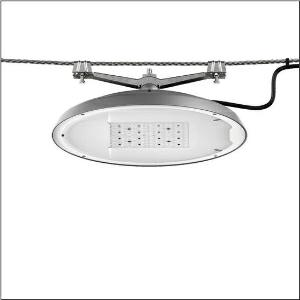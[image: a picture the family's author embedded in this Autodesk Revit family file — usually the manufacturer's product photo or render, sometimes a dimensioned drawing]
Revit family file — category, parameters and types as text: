
# Revit family: dl_r__50_iq_mini___st0_8s_5xa248v31f08me_3f47
name_source: partatom
category: Lighting Fixtures
units: mm (PartAtom-declared; Revit-internal decimal feet)

## family parameters
Cut with Voids When Loaded = No
Host = Face
Light Source = No
Part Type = Normal
Room Calculation Point = No
Round Connector Dimension = Use Diameter
Shared = No

## types (1)
- --- (1 x LED, 15660 lm, 107.8 W, 3000K)
    Apparent Load = 108 VA
    CIE Flux Codes = 38 75 97 100 100
    Color Rendering = 70
    Color Temperature = 3000K
    Default Elevation = 1800 mm
    Description = DL® 50 iQ mini, catenary luminaire, primary light control with lens, of PMMA, primary optical cover: cover, of toughened safety glass, transparent, light distribution: ST0.8s, light emission: direct distribution, primary light characteristic: symmetric, installation type: suspended mounting, LED, High Power LED, rated luminous flux: 15.660lm, luminous efficacy: 145lm/W, light colour: 730, colour temperature: 3000K, control: optimised constant luminous flux control (CLO 2.0), Desk-Remote (wireless, voltage-free reading and setting of iQ features in the workshop via application-optimized NFC function/RFID function), Light-Fading, Smart-Wire, Night-Set, Lumen-Switch, Temp-Guard, Auto-Match, Street-Remote, mains connection: 230..240V, AC, 50/60Hz, start of lifetime: 108W, end of service life: 118W, reduction: 47W, luminaire housing, of diecast aluminium, powder-coated, Siteco® metallic grey (DB 702S), diameter: 500mm, height: 115mm, protection rating (complete): IP66, insulation class (complete): insulation class II (safety insulation), certification: CE, ENEC, VDE, impact resistance: IK08, permissible operating ambient temperature for outdoor applications: -25..+40°C, standard-compliant lighting for roads and squares, packaging unit: 1 piece

Light Distribution: ST0.8s
    Height = 124 mm  [stored 0.406824 ft]
    Lamp = 1 x LED
    Lamp Light Flux = 15660 lm
    Lamp Power = 107.8 W
    Lamp count = 1
    Length = 500 mm
    Luminous efficacy = 145 lm/W
    Manufacturer = Siteco
    ModVariant = No
    Model = 5XA248V31F08ME
    Number of Poles = 1
    OnlyDefault = Yes
    Power Factor = 1
    Product Name = DL® 50 iQ mini | ST0.8s
    Product group = catenary luminaire
    ProductGroupID = 6300
    Protection Class = Protection class II
    Protection Degree = IP 66
    RLX_Detail_Level = 1
    RLX_Emergency_Light_Flux = 0 lm
    RLX_Emergency_Type = 0
    RLX_Emergency_Type_DB = No
    RlxData = <blob elided: 127109 chars, md5=ac68785f>
    Socket = socket
    Standby Power = 0 W
    System Light Flux = 15660 lm
    System Power = 108 W
    Type Comments = factory setting: luminous flux: 100 % | dim-lin: 254 | 565 mA
    Type Image = l_1251783.jpg
    URL = http://relux.com
    VarID = @adj_090351
    Voltage = 0 V
    Weight = 0.00 kg
    Width = 0 mm  [stored 0 ft]

note: [stored X ft] marks values corroborated as IEEE doubles in the binary element streams (Revit-internal decimal feet)

## geometry (parser evidence)
native form markers: Blend x4, Sweep x15
no freeform markers — native parametric forms only
